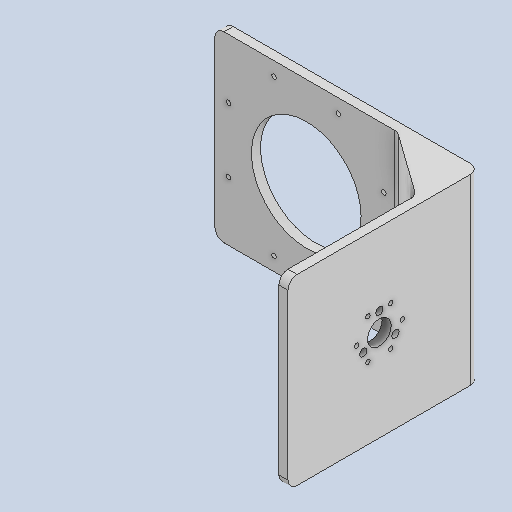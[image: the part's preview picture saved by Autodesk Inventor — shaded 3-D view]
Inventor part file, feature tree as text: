
AUTODESK INVENTOR PART (.ipt)
format: ipt  version: 2024.3 (Build 283343000, 343)  size: 239,616 bytes
history: native  units: mm
features: sketch x10, extrude x7, hole x3, other x1, fillet x1
ambient origin geometry x8: Origin, YZ Plane, XZ Plane, XY Plane, X Axis, Y Axis, Z Axis, Center Point
bodies: Body1 (feature_tree)
feature tree (22):
  other  "ソリッド1"
  extrude  "押し出し1"  Depth=97.0mm
  hole  "穴1"  [1 undecoded]
  extrude  "押し出し2"  Depth=50.0mm
  extrude  "押し出し3"  Depth=50.0mm
  extrude  "押し出し4"  Depth=50.0mm
  hole  "穴2"  [1 undecoded]
  hole  "穴3"  [1 undecoded]
  extrude  "押し出し5"  TaperAngle=22.5deg  [1 undecoded]
  extrude  "押し出し9"  Depth=80.0mm TaperAngle=360.0deg
  fillet  "フィレット2"  Radius=60.0mm
  extrude  "押し出し12"  Depth=5.0mm TaperAngle=0.0deg
  sketch  "スケッチ1"
  sketch  "スケッチ2"
  sketch  "スケッチ3"
  sketch  "スケッチ4"
  sketch  "スケッチ5"
  sketch  "スケッチ6"
  sketch  "スケッチ7"
  sketch  "スケッチ8"
  sketch  "スケッチ13"
  sketch  "スケッチ16"
note: 4 required parameter values undecoded (feature->parameter linkage not recoverable at this tier; creation-order binding heuristic only, values carry confidence <= 0.55)
